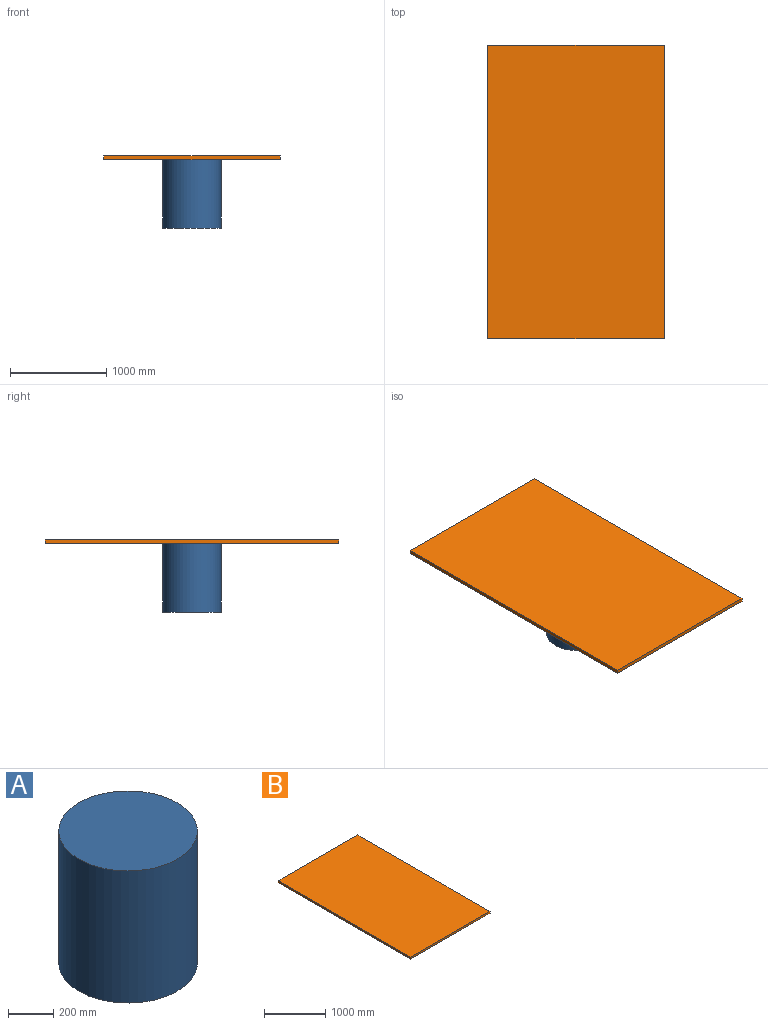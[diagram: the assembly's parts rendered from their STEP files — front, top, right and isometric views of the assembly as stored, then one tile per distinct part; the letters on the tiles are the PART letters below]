
ASSEMBLY  parts=2 mates=1
PART A: 3 faces, bbox 609.6x609.6x711.2 mm
  f0: cylinder r=304.8mm len=711.2mm, axis (0,0,-1), area 1362029.7mm2, adj f1,f2
  f1: plane 609.6x609.6mm, normal (0,0,1), area 291863.5mm2, adj f0
  f2: plane 609.6x609.6mm, normal (0,0,-1), area 291863.5mm2, adj f0
PART B: 6 faces, bbox 1828.8x3048x38.1 mm
  f0: plane 1828.8x38.1mm, normal (0,1,0), area 69677.3mm2, adj f1,f3,f4,f5
  f1: plane 3048x38.1mm, normal (-1,0,0), area 116128.8mm2, adj f0,f2,f4,f5
  f2: plane 1828.8x38.1mm, normal (0,-1,0), area 69677.3mm2, adj f1,f3,f4,f5
  f3: plane 3048x38.1mm, normal (1,0,0), area 116128.8mm2, adj f0,f2,f4,f5
  f4: plane 3048x1828.8mm, normal (0,0,1), area 5574182.4mm2, adj f0,f1,f2,f3
  f5: plane 3048x1828.8mm, normal (0,0,-1), area 5574182.4mm2, adj f0,f1,f2,f3
PLACE A t=(56.26,-383.49,-979.56)mm
PLACE B t=(56.26,-383.49,-268.36)mm
MATE planar B.f5 <-> A.f0  axis (0,0,-1) through (56.26,-383.49,-268.36)mm
